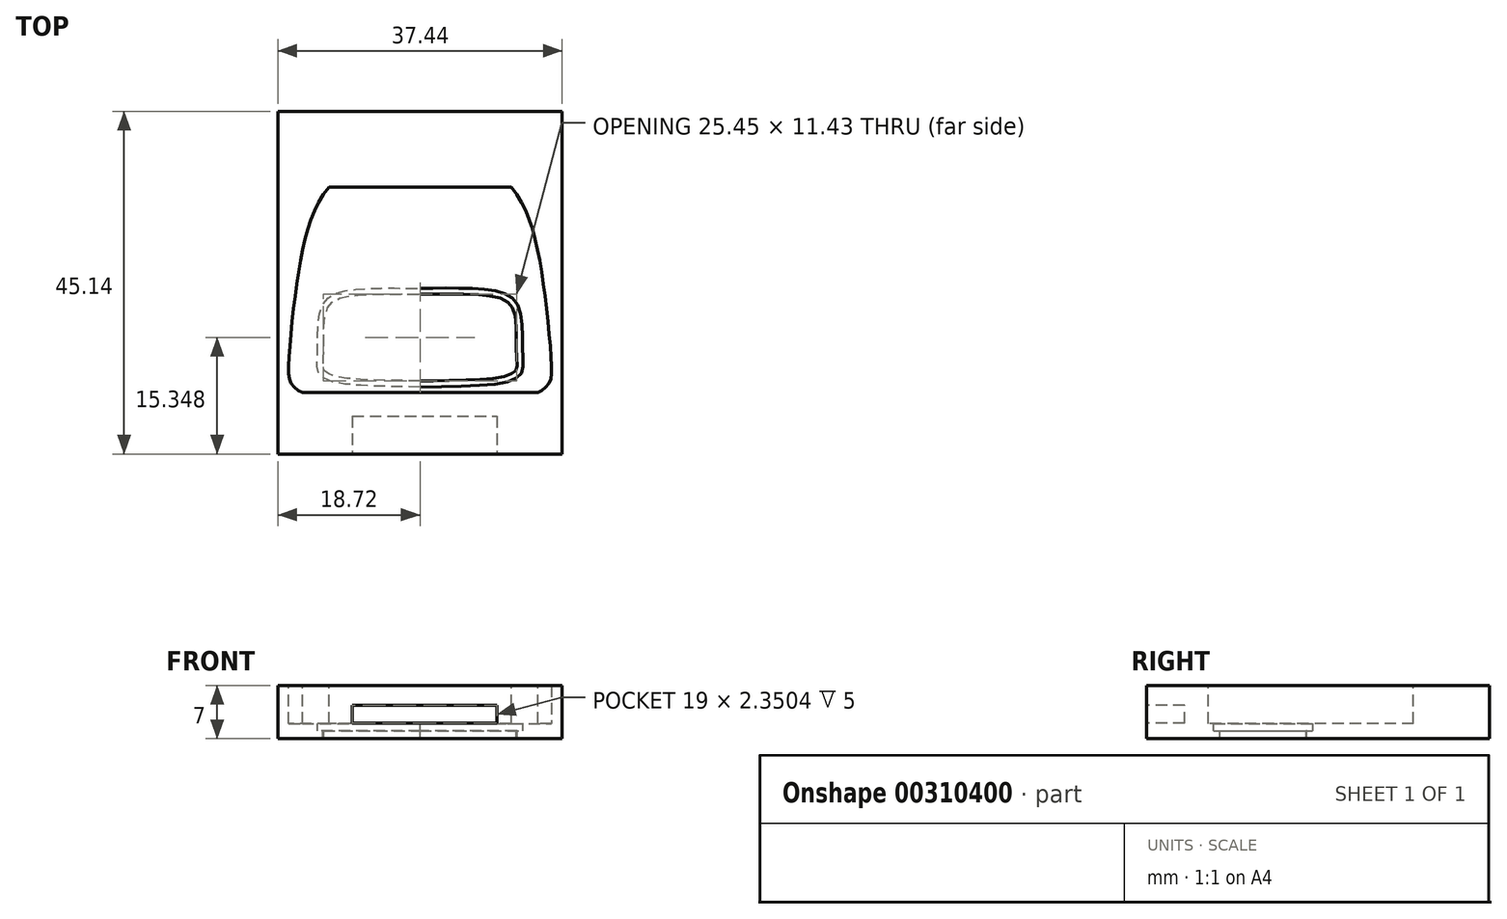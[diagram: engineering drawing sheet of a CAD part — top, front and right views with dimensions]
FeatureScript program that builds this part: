
annotation { "Feature Type Name" : "Feature", "Feature Type Description" : "" }
export const myFeature = defineFeature(function(context is Context, id is Id, definition is map)
    precondition{}
    {
        {
            var Q0;
            Q0=qCreatedBy(makeId("Top.planeOp"),FACE);
            var sketch = newSketch(context, id + "F0", { "sketchPlane" : qUnion([Q0])});
            skLineSegment(sketch, "E0.bottom", {"start": v(-18.72, -22.57) * mm, "end": v(18.72, -22.57) * mm});
            skLineSegment(sketch, "E0.top", {"start": v(-18.72, 22.57) * mm, "end": v(18.72, 22.57) * mm});
            skLineSegment(sketch, "E0.left", {"start": v(-18.72, -22.57) * mm, "end": v(-18.72, 22.57) * mm});
            skLineSegment(sketch, "E0.right", {"start": v(18.72, -22.57) * mm, "end": v(18.72, 22.57) * mm});
            skPoint(sketch, "E0.middle", {"position": v(0, 0) * mm});
            skSolve(sketch);
        }
        {
            var Q0;
            Q0 = qSketchRegion(id + "F0", true);
            extrude(context, id + "F1", {"entities" : qUnion([Q0]), "depth" : 7 * mm});
        }
        {
            var Q0;
            Q0=makeQuery(id+"F1.opExtrude","SWEPT_FACE",FACE,{"disambiguationData":[OSD([sQuery(id+"F0.wireOp",EDGE,"E0.bottom")])]});
            var sketch = newSketch(context, id + "F2", { "sketchPlane" : qUnion([Q0])});
            skLineSegment(sketch, "E1.bottom", {"start": v(-8.9, 2.03) * mm, "end": v(10.1, 2.03) * mm});
            skLineSegment(sketch, "E1.top", {"start": v(-8.9, 4.38) * mm, "end": v(10.1, 4.38) * mm});
            skLineSegment(sketch, "E1.left", {"start": v(-8.9, 2.03) * mm, "end": v(-8.9, 4.38) * mm});
            skLineSegment(sketch, "E1.right", {"start": v(10.1, 2.03) * mm, "end": v(10.1, 4.38) * mm});
            skSolve(sketch);
        }
        {
            var Q0;
            Q0 = qSketchRegion(id + "F2", true);
            extrude(context, id + "F3", {"entities" : qUnion([Q0]), "operationType" : NewBodyOperationType.REMOVE, "oppositeDirection" : true, "depth" : 5 * mm});
        }
        {
            var Q0;
            Q0=makeQuery(id+"F1.opExtrude","CAP_FACE",FACE,{"disambiguationData":[OSD([sQuery(id+"F0.wireOp",EDGE,"E0.bottom"),sQuery(id+"F0.wireOp",EDGE,"E0.top"),sQuery(id+"F0.wireOp",EDGE,"E0.left"),sQuery(id+"F0.wireOp",EDGE,"E0.right")])],"isStart":false});
            var sketch = newSketch(context, id + "F4", { "sketchPlane" : qUnion([Q0])});
            skLineSegment(sketch, "E2", {"start": v(12, 12.57) * mm, "end": v(-12, 12.57) * mm});
            skLineSegment(sketch, "E3", {"start": v(-12, 12.57) * mm, "end": v(0, 12.57) * mm});
            skLineSegment(sketch, "E4", {"start": v(-15.5, -14.43) * mm, "end": v(15.5, -14.43) * mm});
            skLineSegment(sketch, "E5", {"start": v(15.5, -14.43) * mm, "end": v(0, -14.43) * mm});
            skFitSpline(sketch, "E6", {"points": [v(-12, 12.57) * mm, v(-14.83, 6.9) * mm, v(-16.51, -2.33) * mm, v(-17.3, -11.52) * mm, v(-16.84, -13.48) * mm, v(-15.5, -14.43) * mm], "startDerivative": vector(-17.88, -21.07) * mm, "endDerivative": vector(10.53, -3.37) * mm});
            skFitSpline(sketch, "E7.MirrorCS", {"points": [v(12, 12.57) * mm, v(14.83, 6.9) * mm, v(16.51, -2.33) * mm, v(17.3, -11.52) * mm, v(16.84, -13.48) * mm, v(15.5, -14.43) * mm], "startDerivative": vector(17.88, -21.07) * mm, "endDerivative": vector(-10.53, -3.37) * mm});
            skSolve(sketch);
        }
        {
            var Q0;
            Q0 = qSketchRegion(id + "F4", true);
            var Q1;
            Q1=makeQuery(id+"F1.opExtrude","CAP_FACE",FACE,{"disambiguationData":[OSD([sQuery(id+"F0.wireOp",EDGE,"E0.bottom"),sQuery(id+"F0.wireOp",EDGE,"E0.top"),sQuery(id+"F0.wireOp",EDGE,"E0.left"),sQuery(id+"F0.wireOp",EDGE,"E0.right")])],"isStart":true});
            extrude(context, id + "F5", {"entities" : qUnion([Q0, Q1]), "operationType" : NewBodyOperationType.REMOVE, "oppositeDirection" : true, "depth" : 5 * mm});
        }
        {
            var Q0;
            Q0=makeQuery(id+"F5.boolean.opBoolean","COPY",FACE,{"derivedFrom":makeQuery(id+"F5.opExtrude","CAP_FACE",FACE,{"disambiguationData":[OSD([sQuery(id+"F4.wireOp",EDGE,"E2"),sQuery(id+"F4.wireOp",EDGE,"E3"),sQuery(id+"F4.wireOp",EDGE,"E4"),sQuery(id+"F4.wireOp",EDGE,"E5"),sQuery(id+"F4.wireOp",EDGE,"E7.MirrorCS"),sQuery(id+"F4.wireOp",EDGE,"E6")])],"isStart":false})});
            var sketch = newSketch(context, id + "F6", { "sketchPlane" : qUnion([Q0])});
            skPoint(sketch, "E8.0.internal.snap0", {"position": v(0, -14.43) * mm});
            skPoint(sketch, "E8.5.internal.snap0", {"position": v(0, -14.43) * mm});
            skFitSpline(sketch, "E8", {"points": [v(0, -13.74) * mm, v(-13.02, -12.32) * mm, v(-13.5, -9.22) * mm, v(-12.83, -2.87) * mm, v(-8.88, -0.92) * mm, v(0, -0.74) * mm], "startDerivative": vector(-66.2, 1.06) * mm, "endDerivative": vector(36.54, 0.05) * mm});
            skFitSpline(sketch, "E9.MirrorCS", {"points": [v(0, -13.74) * mm, v(13.02, -12.32) * mm, v(13.5, -9.22) * mm, v(12.83, -2.87) * mm, v(8.88, -0.92) * mm, v(0, -0.74) * mm], "startDerivative": vector(66.2, 1.06) * mm, "endDerivative": vector(-36.54, 0.05) * mm});
            skFitSpline(sketch, "E10.0", {"points": [v(0.01, -12.94) * mm, v(-1.37, -12.92) * mm, v(-3.38, -12.9) * mm, v(-5.83, -12.84) * mm, v(-7.51, -12.77) * mm, v(-9.03, -12.65) * mm, v(-10.33, -12.49) * mm, v(-11.21, -12.3) * mm, v(-11.77, -12.13) * mm, v(-12.1, -11.98) * mm, v(-12.36, -11.84) * mm, v(-12.51, -11.71) * mm, v(-12.6, -11.6) * mm, v(-12.67, -11.47) * mm, v(-12.72, -11.3) * mm, v(-12.77, -10.97) * mm, v(-12.77, -10.42) * mm, v(-12.72, -9.7) * mm, v(-12.7, -9.02) * mm, v(-12.68, -8.32) * mm, v(-12.68, -7.42) * mm, v(-12.67, -6.32) * mm, v(-12.62, -5.26) * mm, v(-12.5, -4.3) * mm, v(-12.31, -3.64) * mm, v(-12.13, -3.23) * mm, v(-11.91, -2.9) * mm, v(-11.58, -2.56) * mm, v(-11.04, -2.23) * mm, v(-10.33, -1.98) * mm, v(-9.46, -1.8) * mm, v(-8.45, -1.66) * mm, v(-6.97, -1.55) * mm, v(-4.93, -1.5) * mm, v(-2.4, -1.52) * mm, v(-0.77, -1.54) * mm, v(0, -1.54) * mm]});
            skFitSpline(sketch, "E10.1", {"points": [v(-0.01, -12.94) * mm, v(1.37, -12.92) * mm, v(3.38, -12.9) * mm, v(5.83, -12.84) * mm, v(7.51, -12.77) * mm, v(9.03, -12.65) * mm, v(10.33, -12.49) * mm, v(11.21, -12.3) * mm, v(11.77, -12.13) * mm, v(12.1, -11.98) * mm, v(12.36, -11.84) * mm, v(12.51, -11.71) * mm, v(12.6, -11.6) * mm, v(12.67, -11.47) * mm, v(12.72, -11.3) * mm, v(12.77, -10.97) * mm, v(12.77, -10.42) * mm, v(12.72, -9.7) * mm, v(12.7, -9.02) * mm, v(12.68, -8.32) * mm, v(12.68, -7.42) * mm, v(12.67, -6.32) * mm, v(12.62, -5.26) * mm, v(12.5, -4.3) * mm, v(12.31, -3.64) * mm, v(12.13, -3.23) * mm, v(11.91, -2.9) * mm, v(11.58, -2.56) * mm, v(11.04, -2.23) * mm, v(10.33, -1.98) * mm, v(9.46, -1.8) * mm, v(8.45, -1.66) * mm, v(6.97, -1.55) * mm, v(4.93, -1.5) * mm, v(2.4, -1.52) * mm, v(0.77, -1.54) * mm, v(0, -1.54) * mm]});
            skSolve(sketch);
        }
        {
            var Q0;
            Q0=makeQuery(id+"F6.imprint","IMPRINT",FACE,{"disambiguationData":[TD([[makeQuery(id+"F6.imprint","IMPRINT",EDGE,{"derivedFrom":sQuery(id+"F6.wireOp",EDGE,"E8")}),-1.0]])]});
            extrude(context, id + "F7", {"entities" : qUnion([Q0]), "operationType" : NewBodyOperationType.REMOVE, "oppositeDirection" : true, "depth" : 1 * mm});
        }
        {
            var Q0;
            Q0=makeQuery(id+"F7.boolean.opBoolean","SPLIT",FACE,{"disambiguationData":[TD([makeQuery(id+"F7.opExtrude","SWEPT_FACE",FACE,{"disambiguationData":[OSD([sQuery(id+"F6.wireOp",EDGE,"E10.0")])]})])],"derivedFrom":makeQuery(id+"F5.boolean.opBoolean","COPY",FACE,{"derivedFrom":makeQuery(id+"F5.opExtrude","CAP_FACE",FACE,{"disambiguationData":[OSD([sQuery(id+"F4.wireOp",EDGE,"E2"),sQuery(id+"F4.wireOp",EDGE,"E3"),sQuery(id+"F4.wireOp",EDGE,"E4"),sQuery(id+"F4.wireOp",EDGE,"E5"),sQuery(id+"F4.wireOp",EDGE,"E7.MirrorCS"),sQuery(id+"F4.wireOp",EDGE,"E6")])],"isStart":false})})});
            extrude(context, id + "F8", {"entities" : qUnion([Q0]), "operationType" : NewBodyOperationType.REMOVE, "oppositeDirection" : true, "depth" : 25 * mm});
        }
    });
